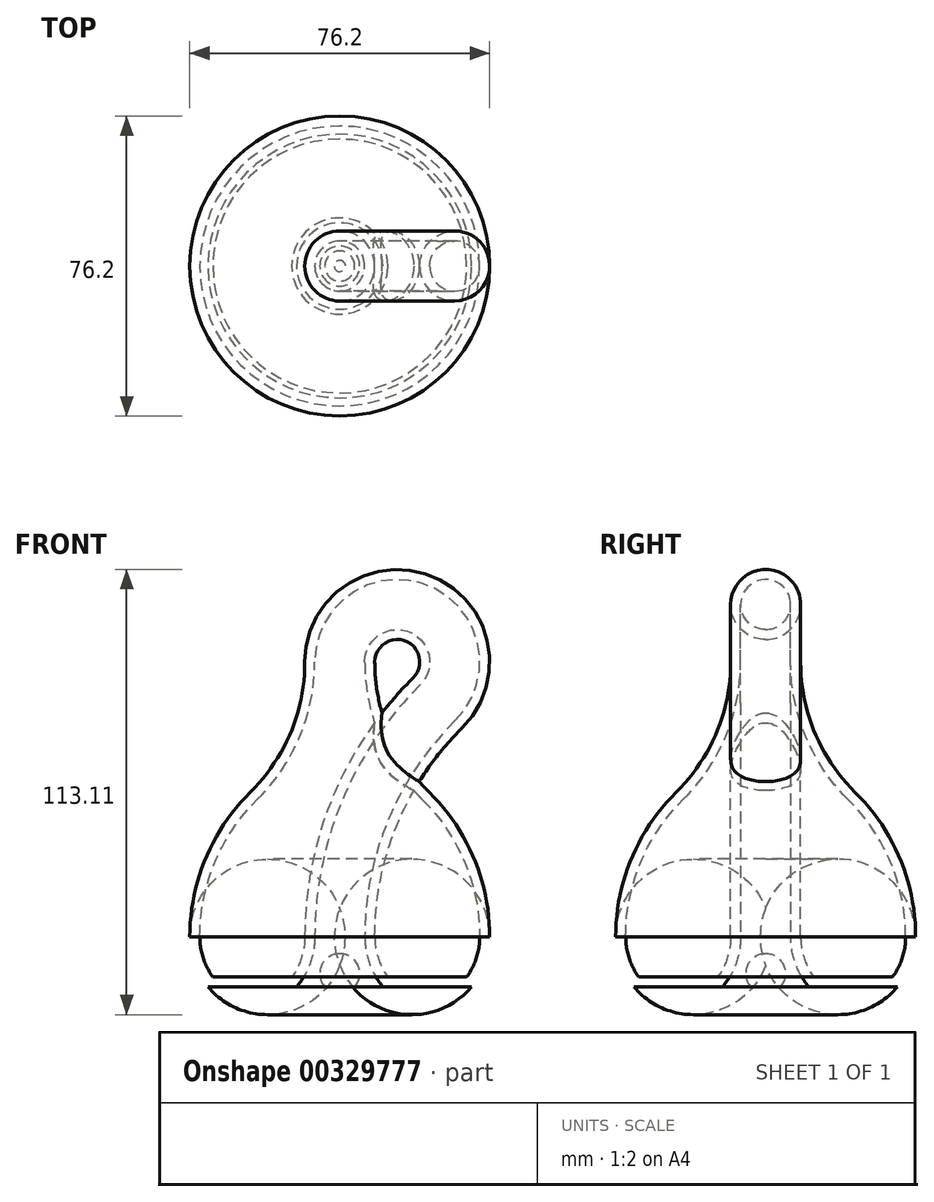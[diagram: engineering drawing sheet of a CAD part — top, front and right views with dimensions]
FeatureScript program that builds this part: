
annotation { "Feature Type Name" : "Feature", "Feature Type Description" : "" }
export const myFeature = defineFeature(function(context is Context, id is Id, definition is map)
    precondition{}
    {
        {
            var Q0;
            Q0=qCreatedBy(makeId("Front.planeOp"),FACE);
            var sketch = newSketch(context, id + "F0", { "sketchPlane" : qUnion([Q0])});
            skArc(sketch, "E0", {"start": v(-38.1, 12.7) * mm, "mid": v(-36.9, 5.94) * mm, "end": v(-33.48, 0) * mm});
            skArc(sketch, "E1", {"start": v(-35.56, 12.7) * mm, "mid": v(-34.7, 7.36) * mm, "end": v(-32.24, 2.54) * mm});
            skArc(sketch, "E2", {"start": v(-10.97, 0) * mm, "mid": v(-7.54, 5.94) * mm, "end": v(-6.35, 12.7) * mm});
            skArc(sketch, "E3", {"start": v(-12.2, 2.54) * mm, "mid": v(-9.74, 7.36) * mm, "end": v(-8.9, 12.7) * mm});
            skLineSegment(sketch, "E4", {"start": v(-32.24, 2.54) * mm, "end": v(-22.23, 2.54) * mm});
            skLineSegment(sketch, "E5", {"start": v(-33.48, 0) * mm, "end": v(-22.23, 0) * mm});
            skLineSegment(sketch, "E6", {"start": v(-38.1, 12.7) * mm, "end": v(-35.56, 12.7) * mm, "construction": true});
            skLineSegment(sketch, "E7", {"start": v(-6.35, 12.7) * mm, "end": v(-8.9, 12.7) * mm});
            skLineSegment(sketch, "E8", {"start": v(0, 24.96) * mm, "end": v(0, -30.9) * mm, "construction": true});
            skArc(sketch, "E9", {"start": v(-22.74, 49.43) * mm, "mid": v(-34.1, 32.6) * mm, "end": v(-38.1, 12.7) * mm});
            skArc(sketch, "E10", {"start": v(-20.96, 47.63) * mm, "mid": v(-31.76, 31.63) * mm, "end": v(-35.56, 12.7) * mm});
            skArc(sketch, "E11", {"start": v(-22.74, 49.43) * mm, "mid": v(-12.5, 64.6) * mm, "end": v(-8.9, 82.55) * mm});
            skArc(sketch, "E12", {"start": v(-20.95, 47.63) * mm, "mid": v(-10.15, 63.62) * mm, "end": v(-6.35, 82.55) * mm});
            skLineSegment(sketch, "E13", {"start": v(-8.9, 82.55) * mm, "end": v(-6.35, 82.55) * mm});
            skLineSegment(sketch, "E14", {"start": v(-6.35, 12.7) * mm, "end": v(0, 12.7) * mm, "construction": true});
            skLineSegment(sketch, "E15", {"start": v(-6.35, 82.55) * mm, "end": v(0, 82.55) * mm, "construction": true});
            skLineSegment(sketch, "E16", {"start": v(-3.81, 0) * mm, "end": v(0, 0) * mm});
            skLineSegment(sketch, "E17", {"start": v(0, 0) * mm, "end": v(0, 8.44) * mm});
            skLineSegment(sketch, "E18", {"start": v(-33.48, 0) * mm, "end": v(-55.34, 26.06) * mm, "construction": true});
            skLineSegment(sketch, "E19", {"start": v(-22.23, 2.54) * mm, "end": v(-12.2, 2.54) * mm});
            skLineSegment(sketch, "E20", {"start": v(-22.23, 0) * mm, "end": v(-10.97, 0) * mm});
            skLineSegment(sketch, "E21", {"start": v(-22.23, 0) * mm, "end": v(-22.23, 2.54) * mm, "construction": true});
            skArc(sketch, "E22", {"start": v(0, 8.44) * mm, "mid": v(-4.63, 5.45) * mm, "end": v(-3.81, 0) * mm});
            skSolve(sketch);
        }
        {
            var Q0;
            Q0 = qSketchRegion(id + "F0", true);
            var Q1;
            Q1=sQuery(id+"F0.wireOp",EDGE,"E8");
            revolve(context, id + "F1", {"entities" : qUnion([Q0]), "axis" : qUnion([Q1]), "revolveType" : RevolveType.FULL});
        }
        {
            var Q0;
            Q0=qCreatedBy(makeId("Front.planeOp"),FACE);
            var sketch = newSketch(context, id + "F2", { "sketchPlane" : qUnion([Q0])});
            skArc(sketch, "E23", {"start": v(29.32, 67.63) * mm, "mid": v(33.94, 74.47) * mm, "end": v(35.56, 82.55) * mm, "construction": true});
            skLineSegment(sketch, "E24", {"start": v(-8.89, 82.55) * mm, "end": v(-6.35, 82.55) * mm, "construction": true});
            skLineSegment(sketch, "E25.0", {"start": v(-6.35, 12.7) * mm, "end": v(0, 12.7) * mm, "construction": true});
            skLineSegment(sketch, "E25.1", {"start": v(-8.9, 12.7) * mm, "end": v(8.9, 12.7) * mm, "construction": true});
            skArc(sketch, "E26.trimOffspring", {"start": v(31.1, 65.82) * mm, "mid": v(36.28, 73.49) * mm, "end": v(38.1, 82.55) * mm, "construction": true});
            skArc(sketch, "E27", {"start": v(20.4, 76.67) * mm, "mid": v(22.22, 79.37) * mm, "end": v(22.86, 82.55) * mm, "construction": true});
            skArc(sketch, "E28", {"start": v(18.62, 78.48) * mm, "mid": v(19.88, 80.35) * mm, "end": v(20.32, 82.55) * mm, "construction": true});
            skArc(sketch, "E29", {"start": v(14.6, 106.04) * mm, "mid": v(-2, 99.16) * mm, "end": v(-8.89, 82.55) * mm, "construction": true});
            skArc(sketch, "E30", {"start": v(14.6, 103.5) * mm, "mid": v(-0.21, 97.37) * mm, "end": v(-6.35, 82.55) * mm, "construction": true});
            skArc(sketch, "E31", {"start": v(14.6, 90.8) * mm, "mid": v(8.77, 88.39) * mm, "end": v(6.35, 82.55) * mm, "construction": true});
            skArc(sketch, "E32", {"start": v(14.6, 88.27) * mm, "mid": v(10.56, 86.6) * mm, "end": v(8.89, 82.55) * mm, "construction": true});
            skArc(sketch, "E33", {"start": v(20.32, 82.55) * mm, "mid": v(18.65, 86.6) * mm, "end": v(14.6, 88.27) * mm, "construction": true});
            skArc(sketch, "E34", {"start": v(22.86, 82.55) * mm, "mid": v(20.44, 88.39) * mm, "end": v(14.6, 90.8) * mm, "construction": true});
            skArc(sketch, "E35", {"start": v(35.56, 82.55) * mm, "mid": v(29.42, 97.37) * mm, "end": v(14.6, 103.5) * mm, "construction": true});
            skArc(sketch, "E36", {"start": v(38.1, 82.55) * mm, "mid": v(31.22, 99.16) * mm, "end": v(14.6, 106.04) * mm, "construction": true});
            skLineSegment(sketch, "E37", {"start": v(-8.89, 82.55) * mm, "end": v(0, 82.55) * mm, "construction": true});
            skLineSegment(sketch, "E38", {"start": v(14.6, 106.04) * mm, "end": v(14.6, 97.16) * mm, "construction": true});
            skArc(sketch, "E39", {"start": v(18.62, 78.48) * mm, "mid": v(-1.74, 48.35) * mm, "end": v(-8.89, 12.7) * mm, "construction": true});
            skArc(sketch, "E40", {"start": v(29.32, 67.63) * mm, "mid": v(12.32, 42.47) * mm, "end": v(6.35, 12.7) * mm, "construction": true});
            skArc(sketch, "E41", {"start": v(31.1, 65.82) * mm, "mid": v(14.67, 41.5) * mm, "end": v(8.9, 12.7) * mm, "construction": true});
            skArc(sketch, "E42", {"start": v(20.4, 76.67) * mm, "mid": v(0.6, 47.37) * mm, "end": v(-6.35, 12.7) * mm, "construction": true});
            skLineSegment(sketch, "E43.trimOffspring", {"start": v(20.32, 82.55) * mm, "end": v(29.21, 82.55) * mm, "construction": true});
            skLineSegment(sketch, "E44", {"start": v(0, 82.55) * mm, "end": v(8.89, 82.55) * mm, "construction": true});
            skLineSegment(sketch, "E45", {"start": v(29.21, 82.55) * mm, "end": v(38.1, 82.55) * mm, "construction": true});
            skLineSegment(sketch, "E46", {"start": v(14.6, 97.16) * mm, "end": v(14.6, 88.27) * mm, "construction": true});
            skLineSegment(sketch, "E47", {"start": v(0, 12.7) * mm, "end": v(6.35, 12.7) * mm, "construction": true});
            skArc(sketch, "E48", {"start": v(24.86, 72.15) * mm, "mid": v(20.24, 96.02) * mm, "end": v(0, 82.55) * mm});
            skArc(sketch, "E49", {"start": v(24.86, 72.15) * mm, "mid": v(6.47, 44.92) * mm, "end": v(0, 12.7) * mm});
            skLineSegment(sketch, "E50.0", {"start": v(-6.35, 82.55) * mm, "end": v(6.35, 82.55) * mm, "construction": true});
            skLineSegment(sketch, "E50.1", {"start": v(-8.89, 82.55) * mm, "end": v(8.89, 82.55) * mm, "construction": true});
            skLineSegment(sketch, "E51.0", {"start": v(-38.1, 12.7) * mm, "end": v(38.1, 12.7) * mm, "construction": true});
            skLineSegment(sketch, "E52", {"start": v(38.1, 12.7) * mm, "end": v(38.1, 82.55) * mm, "construction": true});
            skSolve(sketch);
        }
        {
            var Q0;
            Q0=makeQuery(id+"F1.opRevolve","SWEPT_FACE",FACE,{"disambiguationData":[OSD([sQuery(id+"F0.wireOp",EDGE,"E13")])]});
            var sketch = newSketch(context, id + "F3", { "sketchPlane" : qUnion([Q0])});
            skCircle(sketch, "E53.0", {"center": v(0, 0) * mm, "radius": 6.35 * mm});
            skCircle(sketch, "E53.1", {"center": v(0, 0) * mm, "radius": 8.89 * mm});
            skSolve(sketch);
        }
        {
            var Q0;
            Q0=makeQuery(id+"F3.imprint","IMPRINT",FACE,{"disambiguationData":[TD([[makeQuery(id+"F3.imprint","IMPRINT",EDGE,{"derivedFrom":sQuery(id+"F3.wireOp",EDGE,"E53.0")}),1.0]])]});
            var Q1;
            Q1=sQuery(id+"F3.wireOp",EDGE,"E53.0");
            var Q2;
            Q2=sQuery(id+"F2.wireOp",EDGE,"E48");
            var Q3;
            Q3=sQuery(id+"F2.wireOp",EDGE,"E49");
            sweep(context, id + "F4", {"operationType" : NewBodyOperationType.REMOVE, "profiles" : qUnion([Q0]), "surfaceProfiles" : qUnion([Q1]), "path" : qUnion([Q2, Q3])});
        }
        {
            var Q0;
            Q0=makeQuery(id+"F1.opRevolve","SWEPT_FACE",FACE,{"disambiguationData":[OSD([sQuery(id+"F0.wireOp",EDGE,"E13")])]});
            var Q1;
            Q1=sQuery(id+"F2.wireOp",EDGE,"E48");
            var Q2;
            Q2=sQuery(id+"F2.wireOp",EDGE,"E49");
            sweep(context, id + "F5", {"operationType" : NewBodyOperationType.ADD, "profiles" : qUnion([Q0]), "path" : qUnion([Q1, Q2])});
        }
    });
